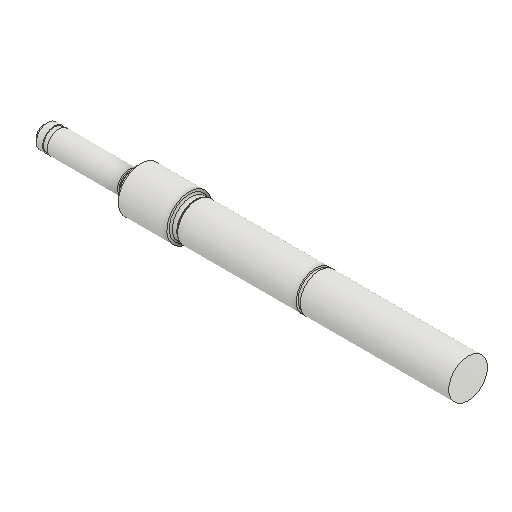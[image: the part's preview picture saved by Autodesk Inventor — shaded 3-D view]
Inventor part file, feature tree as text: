
AUTODESK INVENTOR PART (.ipt)
format: ipt  version: 2025.1 (Build 291241000, 241)  size: 173,056 bytes
history: native  units: mm
features: other x13, chamfer x2, revolve x1
ambient origin geometry x6: Origin, XZ Plane, XY Plane, X Axis, Y Axis, Z Axis
bodies: Body1 (feature_tree)
feature tree (16):
  other  "{BB8FE430-83BF-418D-8DF9-9B323D3DB9B9}"
  other  "Bryła1"
  revolve  "Obrót1"
  other  "Rowek dla pierścienia zabezpieczającego2"
  chamfer  "Faza4"  [1 undecoded]
  chamfer  "Faza1"  Distance=3.0mm
  other  "Podcięcie1"
  other  "Podcięcie2"
  other  "Rowek dla pierścienia zabezpieczającego1"
  other  "Płaszczyzna początkowa"
  other  "Punkt początkowy"
  other  "Szkic główny"
  other  "iFeature2:1"
  other  "iFeature2:2"
  other  "iFeature27:1"
  other  "iFeature27:2"
note: 1 required parameter value undecoded (feature->parameter linkage not recoverable at this tier; creation-order binding heuristic only, values carry confidence <= 0.55)
